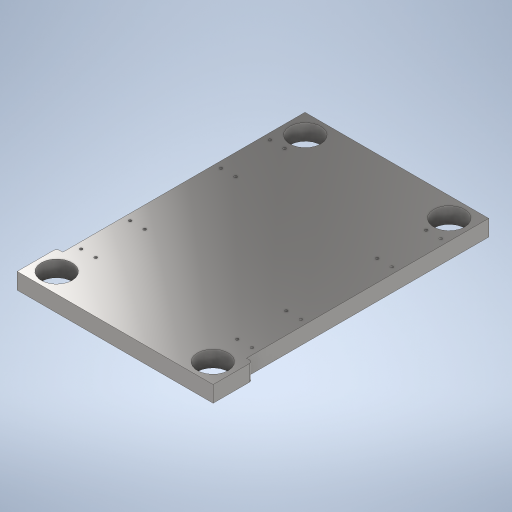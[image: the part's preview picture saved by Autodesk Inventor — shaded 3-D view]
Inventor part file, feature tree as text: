
AUTODESK INVENTOR PART (.ipt)
format: ipt  version: 2023 (Build 270158000, 158)  size: 375,296 bytes
history: native  units: in
note: dims shown in document units (in); Inventor stores cm internally (conversion verified against a paired STEP export)
features: extrude x3, sketch x3, hole x1, fillet x1
ambient origin geometry x8: Origin, YZ Plane, XZ Plane, XY Plane, X Axis, Y Axis, Z Axis, Center Point
bodies: Solid1 (feature_tree)
feature tree (8):
  extrude  "Extrusion1"  Depth=11.5in
  extrude  "Extrusion2"  Depth=0.66in
  hole  "Hole1"  [1 undecoded]
  extrude  "Extrusion10"  Depth=0.25in
  fillet  "Fillet5"  Radius=1.258in
  sketch  "Sketch1"  dims[d0=7.5in d1=11.5in]
  sketch  "Sketch7"  dims[d2=0.66in d3=0.0in d5=0.8in]
  sketch  "Sketch11"  dims[d7=0.8in d9=0.8in d11=0.8in d12=1.258in d14=1.258in d15=1.258in d16=0.0in d17=0.0in d167=1.0in d168=1.0in d169=3.7105in d172=0.3in d173=0.3in d174=0.3in d175=0.3in d176=0.3in d177=0.3in d178=0.3in d179=0.3in d182=1.0in d183=1.0in d184=3.7105in d185=1.0in d186=1.0in d187=0.3in d188=0.3in d189=0.3in d190=0.3in d191=0.3in d192=0.3in d193=0.3in d194=0.3in d195=0.1378in d196=0.1378in d197=0.1378in d198=0.1378in d199=0.1378in d200=0.1378in d201=0.1378in d202=0.1378in d203=0.1378in d204=0.1378in d205=0.1378in d206=0.1378in d207=0.1378in d208=0.1378in d209=0.1378in d210=0.1378in d245=0.1122in d246=0.6in d247=0.185in d248=0.25in d249=0.5635in d250=1.0in d251=0.8108in d258=6.375in d259=0.25in d260=0.25in d264=1.258in d266=0.8125in d267=0.8125in d268=0.66in d269=0.0in d271=0.125in d272=0.25in d273=0.25in d274=0.8125in d276=0.8125in]
note: 1 required parameter value undecoded (feature->parameter linkage not recoverable at this tier; creation-order binding heuristic only, values carry confidence <= 0.55)
